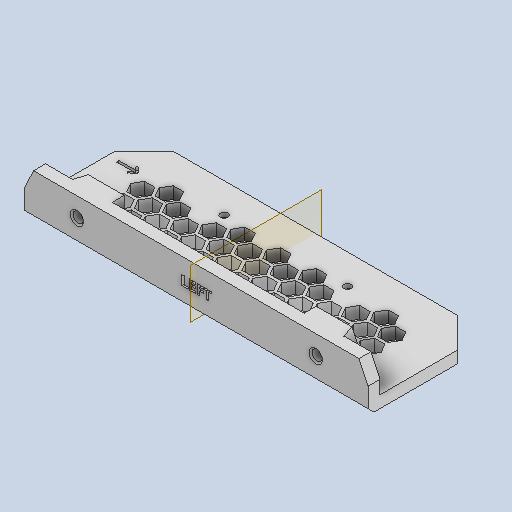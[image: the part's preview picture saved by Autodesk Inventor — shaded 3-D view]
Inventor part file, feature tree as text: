
AUTODESK INVENTOR PART (.ipt)
format: ipt  version: 2023 (Build 270158000, 158)  size: 610,816 bytes
history: native  units: mm
features: other x3, emboss x1, sketch x1, projected_geometry x1
ambient origin geometry x8: Origin, YZ Plane, XZ Plane, XY Plane, X Axis, Y Axis, Z Axis, Center Point
bodies: Solid1 (feature_tree)
feature tree (6):
  other  "A-01_MIR.ipt"
  emboss  "Emboss1"
  other  "Solid1::A-01_MIR.ipt"
  other  "TaggingFeature1"
  sketch  "Sketch1"  dims[d0=10.0mm d1=1.0mm d2=0.0mm]
  projected_geometry  "Projected Loop1"
